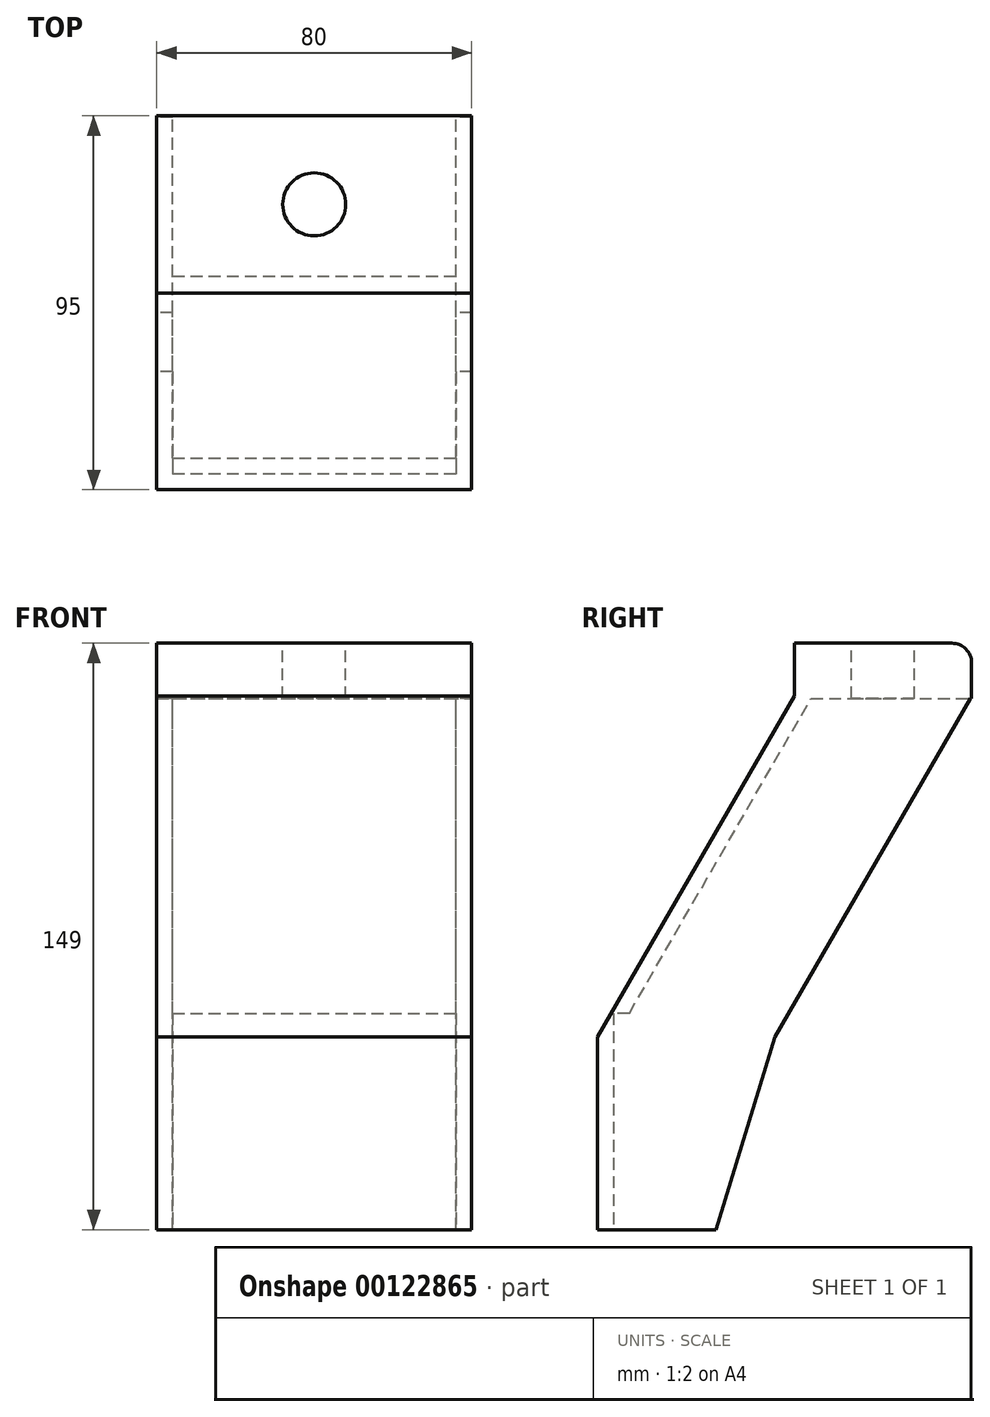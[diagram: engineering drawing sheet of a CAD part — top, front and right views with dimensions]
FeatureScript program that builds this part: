
annotation { "Feature Type Name" : "Feature", "Feature Type Description" : "" }
export const myFeature = defineFeature(function(context is Context, id is Id, definition is map)
    precondition{}
    {
        {
            var Q0;
            Q0=qCreatedBy(makeId("Right.planeOp"),FACE);
            var sketch = newSketch(context, id + "F0", { "sketchPlane" : qUnion([Q0])});
            skLineSegment(sketch, "E0", {"start": v(0, 0) * mm, "end": v(0, -49) * mm});
            skLineSegment(sketch, "E1", {"start": v(0, 0) * mm, "end": v(0, 30) * mm});
            skLineSegment(sketch, "E2", {"start": v(0, 0) * mm, "end": v(50, 86.6) * mm});
            skLineSegment(sketch, "E3", {"start": v(50, 86.6) * mm, "end": v(95, 86.6) * mm});
            skLineSegment(sketch, "E4", {"start": v(0, 0) * mm, "end": v(45, 0) * mm});
            skLineSegment(sketch, "E5", {"start": v(45, 0) * mm, "end": v(95, 86.6) * mm});
            skLineSegment(sketch, "E6", {"start": v(45, 0) * mm, "end": v(45, -49) * mm});
            skLineSegment(sketch, "E7", {"start": v(45, -49) * mm, "end": v(0, -49) * mm});
            skSolve(sketch);
        }
        {
            var Q0;
            Q0=qSketchRegion(id+"F0",true);
            extrude(context, id + "F1", {"entities" : qUnion([Q0]), "depth" : 80 * mm});
        }
        {
            var Q0;
            Q0=makeQuery(id+"F1.opExtrude","SWEPT_FACE",FACE,{"disambiguationData":[OSD([sQuery(id+"F0.wireOp",EDGE,"E5")])]});
            var sketch = newSketch(context, id + "F2", { "sketchPlane" : qUnion([Q0])});
            skLineSegment(sketch, "E8.0", {"start": v(-4, 22.5) * mm, "end": v(-4, 117.5) * mm});
            skLineSegment(sketch, "E8.2", {"start": v(-76, 7.5) * mm, "end": v(-76, 117.5) * mm});
            skLineSegment(sketch, "E9", {"start": v(-76, 117.5) * mm, "end": v(-76, 122.5) * mm});
            skLineSegment(sketch, "E10", {"start": v(-4, 117.5) * mm, "end": v(-4, 122.5) * mm});
            skLineSegment(sketch, "E11", {"start": v(-76, 7.5) * mm, "end": v(-76, -7.5) * mm});
            skLineSegment(sketch, "E12", {"start": v(-76, -7.5) * mm, "end": v(-4, -7.5) * mm});
            skLineSegment(sketch, "E13", {"start": v(-4, -7.5) * mm, "end": v(-4, 22.5) * mm});
            skSolve(sketch);
        }
        {
            var Q0;
            Q0=qSketchRegion(id+"F2",true);
            var Q1;
            Q1=makeQuery(id+"F2.imprint","IMPRINT",FACE,{"disambiguationData":[TD([[makeQuery(id+"F2.imprint","IMPRINT",EDGE,{"derivedFrom":sQuery(id+"F2.wireOp",EDGE,"E8.0")}),1.0]])]});
            extrude(context, id + "F3", {"entities" : qUnion([Q0, Q1]), "operationType" : NewBodyOperationType.REMOVE, "oppositeDirection" : true, "depth" : 35 * mm});
        }
        {
            var Q0;
            Q0=makeQuery(id+"F1.opExtrude","SWEPT_FACE",FACE,{"disambiguationData":[OSD([sQuery(id+"F0.wireOp",EDGE,"E7")])]});
            var sketch = newSketch(context, id + "F4", { "sketchPlane" : qUnion([Q0])});
            skLineSegment(sketch, "E14.0", {"start": v(76, -45) * mm, "end": v(76, -4) * mm});
            skLineSegment(sketch, "E14.1", {"start": v(76, -4) * mm, "end": v(4, -4) * mm});
            skLineSegment(sketch, "E14.2", {"start": v(4, -45) * mm, "end": v(4, -4) * mm});
            skLineSegment(sketch, "E15", {"start": v(4, -45) * mm, "end": v(76, -45) * mm});
            skSolve(sketch);
        }
        {
            var Q0;
            Q0=qSketchRegion(id+"F4",true);
            extrude(context, id + "F5", {"entities" : qUnion([Q0]), "operationType" : NewBodyOperationType.REMOVE, "oppositeDirection" : true, "depth" : 55 * mm});
        }
        {
            var Q0;
            Q0=makeQuery(id+"F3.boolean.opBoolean","COPY",FACE,{"derivedFrom":makeQuery(id+"F3.opExtrude","SWEPT_FACE",FACE,{"disambiguationData":[OSD([sQuery(id+"F0.wireOp",EDGE,"E4"),sQuery(id+"F0.wireOp",EDGE,"E5"),sQuery(id+"F0.wireOp",EDGE,"E6")])]})});
            var sketch = newSketch(context, id + "F6", { "sketchPlane" : qUnion([Q0])});
            skLineSegment(sketch, "E16.0", {"start": v(76, 3.97) * mm, "end": v(4, 3.97) * mm});
            skLineSegment(sketch, "E17.0", {"start": v(4, 3.97) * mm, "end": v(4, 26.97) * mm});
            skLineSegment(sketch, "E18.0", {"start": v(4, 26.97) * mm, "end": v(76, 26.97) * mm});
            skLineSegment(sketch, "E19.0", {"start": v(76, 3.97) * mm, "end": v(76, 26.97) * mm});
            skSolve(sketch);
        }
        {
            var Q0;
            Q0=qSketchRegion(id+"F6",true);
            extrude(context, id + "F7", {"entities" : qUnion([Q0]), "operationType" : NewBodyOperationType.REMOVE, "oppositeDirection" : true, "depth" : 15 * mm});
        }
        {
            var Q0;
            Q0=qCreatedBy(makeId("Top.planeOp"),FACE);
            cPlane(context, id + "F8", {"entities" : qUnion([Q0]), "cplaneType" : CPlaneType.OFFSET, "offset" : 100 * mm, "width" : 150 * mm, "height" : 150 * mm});
        }
        {
            var Q0;
            Q0=qCreatedBy(id+"F8.planeOp",FACE);
            var sketch = newSketch(context, id + "F9", { "sketchPlane" : qUnion([Q0])});
            skLineSegment(sketch, "E20.0", {"start": v(80, 50) * mm, "end": v(0, 50) * mm});
            skLineSegment(sketch, "E21.0", {"start": v(0, 50) * mm, "end": v(0, 95) * mm});
            skLineSegment(sketch, "E22.0", {"start": v(80, 50) * mm, "end": v(80, 95) * mm});
            skLineSegment(sketch, "E23", {"start": v(0, 95) * mm, "end": v(80, 95) * mm});
            skCircle(sketch, "E24", {"center": v(40, 72.5) * mm, "radius": 8 * mm});
            skSolve(sketch);
        }
        {
            var Q0;
            Q0=qSketchRegion(id+"F9",true);
            extrude(context, id + "F10", {"entities" : qUnion([Q0]), "operationType" : NewBodyOperationType.ADD, "oppositeDirection" : true, "depth" : 14 * mm});
        }
        {
            var Q0;
            Q0=makeQuery(id+"F10.opExtrude","CAP_EDGE",EDGE,{"disambiguationData":[OSD([sQuery(id+"F9.wireOp",EDGE,"E23")])],"isStart":true});
            fillet(context, id + "F11", {"entities" : qUnion([Q0]), "radius" : 5 * mm, "tangentPropagation" : true, "allowEdgeOverflow" : false});
        }
        {
            var Q0;
            Q0=makeQuery(id+"F10.boolean.opBoolean","MERGE",FACE,{"derivedFrom":[makeQuery(id+"F1.opExtrude","CAP_FACE",FACE,{"disambiguationData":[OSD([sQuery(id+"F0.wireOp",EDGE,"E0"),sQuery(id+"F0.wireOp",EDGE,"E2"),sQuery(id+"F0.wireOp",EDGE,"E3"),sQuery(id+"F0.wireOp",EDGE,"E5"),sQuery(id+"F0.wireOp",EDGE,"E6"),sQuery(id+"F0.wireOp",EDGE,"E7")])],"isStart":true}),makeQuery(id+"F10.opExtrude","SWEPT_FACE",FACE,{"disambiguationData":[OSD([sQuery(id+"F9.wireOp",EDGE,"E21.0")])]})]});
            var sketch = newSketch(context, id + "F12", { "sketchPlane" : qUnion([Q0])});
            skLineSegment(sketch, "E25", {"start": v(0, 0) * mm, "end": v(-45, 0) * mm});
            skLineSegment(sketch, "E26", {"start": v(0, 0) * mm, "end": v(0, -49) * mm});
            skLineSegment(sketch, "E27", {"start": v(0, -49) * mm, "end": v(-30, -49) * mm});
            skLineSegment(sketch, "E28", {"start": v(-30, -49) * mm, "end": v(-45, 0) * mm});
            skLineSegment(sketch, "E29", {"start": v(-45, 0) * mm, "end": v(-45, -49) * mm});
            skLineSegment(sketch, "E30", {"start": v(-45, -49) * mm, "end": v(-30, -49) * mm});
            skSolve(sketch);
        }
        {
            var Q0;
            Q0=makeQuery(id+"F12.imprint","IMPRINT",FACE,{"disambiguationData":[TD([[makeQuery(id+"F12.imprint","IMPRINT",EDGE,{"derivedFrom":sQuery(id+"F12.wireOp",EDGE,"E28")}),1.0]])]});
            extrude(context, id + "F13", {"entities" : qUnion([Q0]), "operationType" : NewBodyOperationType.REMOVE, "oppositeDirection" : true, "depth" : 80 * mm});
        }
    });
